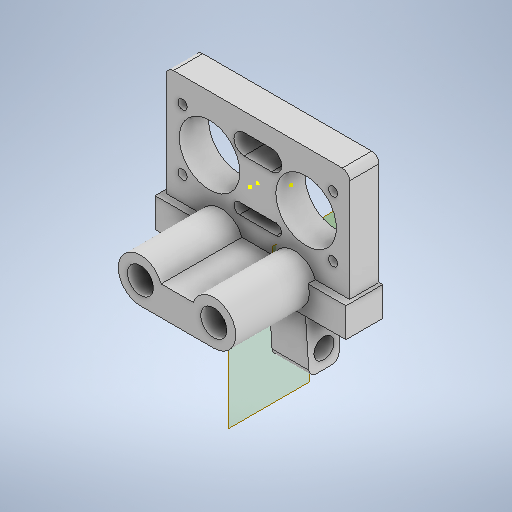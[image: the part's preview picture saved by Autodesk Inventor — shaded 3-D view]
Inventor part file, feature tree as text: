
AUTODESK INVENTOR PART (.ipt)
format: ipt  version: 2025.2 (Build 292293000, 293)  size: 439,296 bytes
history: native  units: mm
features: sketch x13, extrude x9, other x4, mirror x3, fillet x2, hole x1
ambient origin geometry x8: Origin, YZ Plane, XZ Plane, XY Plane, X Axis, Y Axis, Z Axis, Center Point
bodies: Body1 (feature_tree)
feature tree (32):
  other  "Bryła1"
  extrude  "Wyciągnięcie proste1"  Depth=50.0mm
  hole  "Otwór2"  [1 undecoded]
  extrude  "Wyciągnięcie proste3"  Depth=8.0mm TaperAngle=0.0deg
  mirror  "Odbij1"
  extrude  "Wyciągnięcie proste4"  Depth=41.0mm
  fillet  "Zaokrąglenie1"  Radius=16.5mm
  extrude  "Wyciągnięcie proste5"  Depth=45.0mm
  other  "Płaszczyzna konstrukcyjna3"
  other  "Płaszczyzna konstrukcyjna2"
  other  "Płaszczyzna konstrukcyjna1"
  extrude  "Wyciągnięcie proste13"  Depth=20.0mm
  sketch  "Szkic23"
  sketch  "Szkic24"
  extrude  "Wyciągnięcie proste14"  Depth=16.5mm
  mirror  "Odbij4"
  sketch  "Szkic26"
  extrude  "Wyciągnięcie proste15"  Depth=9.35mm
  extrude  "Wyciągnięcie proste16"  Depth=10.0mm
  fillet  "Zaokrąglenie4"  Radius=8.0mm
  mirror  "Odbij5"
  extrude  "Wyciągnięcie proste17"  Depth=45.0mm
  sketch  "Szkic1"
  sketch  "Szkic8"
  sketch  "Szkic9"
  sketch  "Szkic10"
  sketch  "Szkic11"
  sketch  "Szkic22"
  sketch  "Szkic25"
  sketch  "Szkic27"
  sketch  "Szkic28"
  sketch  "Szkic29"
note: 1 required parameter value undecoded (feature->parameter linkage not recoverable at this tier; creation-order binding heuristic only, values carry confidence <= 0.55)
